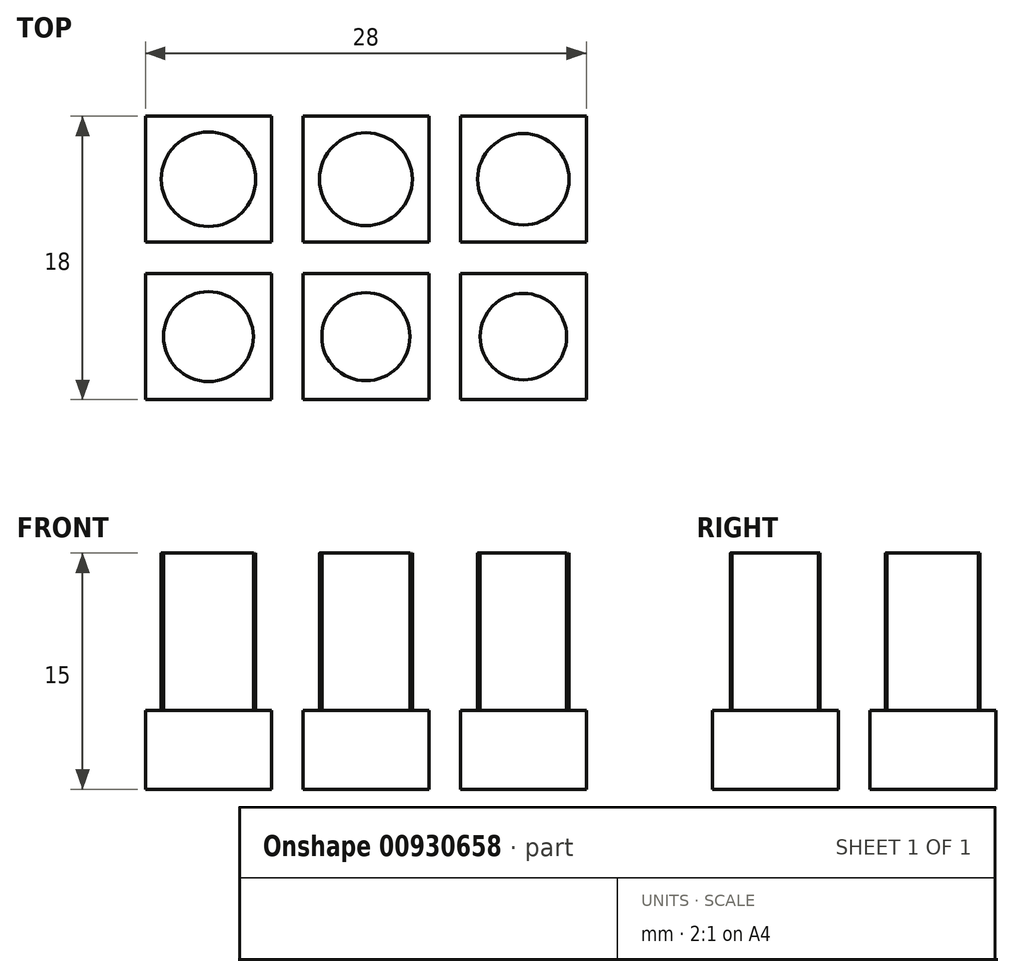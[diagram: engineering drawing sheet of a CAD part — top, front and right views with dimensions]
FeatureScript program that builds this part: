
annotation { "Feature Type Name" : "Feature", "Feature Type Description" : "" }
export const myFeature = defineFeature(function(context is Context, id is Id, definition is map)
    precondition{}
    {
        {
            var Q0;
            Q0=qCreatedBy(makeId("Top.planeOp"),FACE);
            var sketch = newSketch(context, id + "F0", { "sketchPlane" : qUnion([Q0])});
            skLineSegment(sketch, "E0.bottom", {"start": v(0, 0) * mm, "end": v(8, 0) * mm});
            skLineSegment(sketch, "E0.top", {"start": v(0, 8) * mm, "end": v(8, 8) * mm});
            skLineSegment(sketch, "E0.left", {"start": v(0, 0) * mm, "end": v(0, 8) * mm});
            skLineSegment(sketch, "E0.right", {"start": v(8, 0) * mm, "end": v(8, 8) * mm});
            skLineSegment(sketch, "E1", {"start": v(4, 8) * mm, "end": v(4, 0) * mm, "construction": true});
            skLineSegment(sketch, "E2", {"start": v(0, 4) * mm, "end": v(8, 4) * mm, "construction": true});
            skLineSegment(sketch, "E3.bottom", {"start": v(-2, 8) * mm, "end": v(-10, 8) * mm});
            skLineSegment(sketch, "E3.top", {"start": v(-2, 0) * mm, "end": v(-10, 0) * mm});
            skLineSegment(sketch, "E3.left", {"start": v(-2, 8) * mm, "end": v(-2, 0) * mm});
            skLineSegment(sketch, "E3.right", {"start": v(-10, 8) * mm, "end": v(-10, 0) * mm});
            skLineSegment(sketch, "E4.bottom", {"start": v(-12, 8) * mm, "end": v(-20, 8) * mm});
            skLineSegment(sketch, "E4.top", {"start": v(-12, 0) * mm, "end": v(-20, 0) * mm});
            skLineSegment(sketch, "E4.left", {"start": v(-12, 8) * mm, "end": v(-12, 0) * mm});
            skLineSegment(sketch, "E4.right", {"start": v(-20, 8) * mm, "end": v(-20, 0) * mm});
            skLineSegment(sketch, "E5.bottom", {"start": v(0, 10) * mm, "end": v(8, 10) * mm});
            skLineSegment(sketch, "E5.top", {"start": v(0, 18) * mm, "end": v(8, 18) * mm});
            skLineSegment(sketch, "E5.left", {"start": v(0, 10) * mm, "end": v(0, 18) * mm});
            skLineSegment(sketch, "E5.right", {"start": v(8, 10) * mm, "end": v(8, 18) * mm});
            skLineSegment(sketch, "E6.bottom", {"start": v(-2, 18) * mm, "end": v(-10, 18) * mm});
            skLineSegment(sketch, "E6.top", {"start": v(-2, 10) * mm, "end": v(-10, 10) * mm});
            skLineSegment(sketch, "E6.left", {"start": v(-2, 18) * mm, "end": v(-2, 10) * mm});
            skLineSegment(sketch, "E6.right", {"start": v(-10, 18) * mm, "end": v(-10, 10) * mm});
            skLineSegment(sketch, "E7.bottom", {"start": v(-12, 18) * mm, "end": v(-20, 18) * mm});
            skLineSegment(sketch, "E7.top", {"start": v(-12, 10) * mm, "end": v(-20, 10) * mm});
            skLineSegment(sketch, "E7.left", {"start": v(-12, 18) * mm, "end": v(-12, 10) * mm});
            skLineSegment(sketch, "E7.right", {"start": v(-20, 18) * mm, "end": v(-20, 10) * mm});
            skLineSegment(sketch, "E8", {"start": v(-20, 14) * mm, "end": v(8, 14) * mm, "construction": true});
            skLineSegment(sketch, "E9", {"start": v(-16, 18) * mm, "end": v(-16, 0) * mm, "construction": true});
            skLineSegment(sketch, "E10", {"start": v(-6, 18) * mm, "end": v(-6, 0) * mm, "construction": true});
            skLineSegment(sketch, "E11", {"start": v(-20, 4) * mm, "end": v(-2, 4) * mm, "construction": true});
            skLineSegment(sketch, "E12", {"start": v(4, 18) * mm, "end": v(4, 10) * mm, "construction": true});
            skSolve(sketch);
        }
        {
            var Q0;
            Q0=qSketchRegion(id+"F0",true);
            extrude(context, id + "F1", {"entities" : qUnion([Q0]), "depth" : 5 * mm, "offsetDistance" : 25 * mm});
        }
        {
            var Q0;
            Q0=makeQuery(id+"F1.opExtrude","CAP_FACE",FACE,{"disambiguationData":[OSD([sQuery(id+"F0.wireOp",EDGE,"E7.bottom"),sQuery(id+"F0.wireOp",EDGE,"E7.top"),sQuery(id+"F0.wireOp",EDGE,"E7.left"),sQuery(id+"F0.wireOp",EDGE,"E7.right")])],"isStart":false});
            var sketch = newSketch(context, id + "F2", { "sketchPlane" : qUnion([Q0])});
            skCircle(sketch, "E13", {"center": v(-16, 14) * mm, "radius": 3 * mm});
            skPoint(sketch, "E13.centerSnap0", {"position": v(-16, 10) * mm});
            skCircle(sketch, "E14", {"center": v(-6, 14) * mm, "radius": 2.95 * mm});
            skCircle(sketch, "E15", {"center": v(4, 14) * mm, "radius": 2.9 * mm});
            skCircle(sketch, "E16", {"center": v(-16, 4) * mm, "radius": 2.85 * mm});
            skCircle(sketch, "E17", {"center": v(-6, 4) * mm, "radius": 2.8 * mm});
            skCircle(sketch, "E18", {"center": v(4, 4) * mm, "radius": 2.75 * mm});
            skSolve(sketch);
        }
        {
            var Q0;
            Q0=qSketchRegion(id+"F2",true);
            extrude(context, id + "F3", {"entities" : qUnion([Q0]), "depth" : 10 * mm, "offsetDistance" : 25 * mm});
        }
    });
